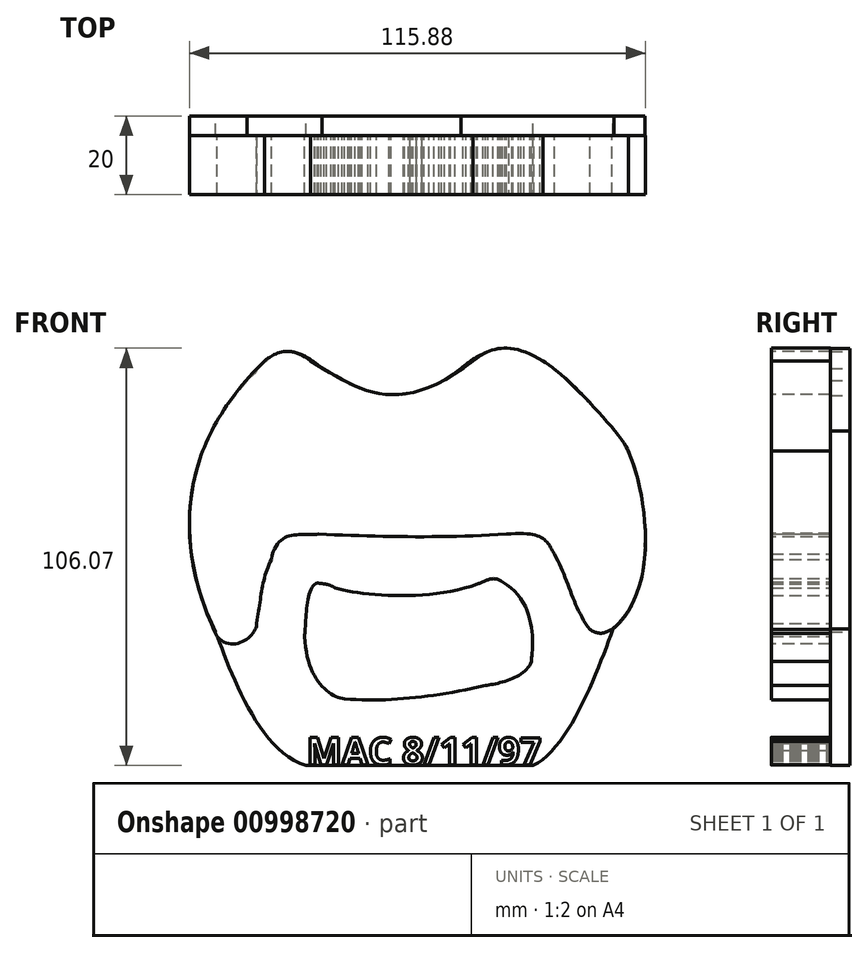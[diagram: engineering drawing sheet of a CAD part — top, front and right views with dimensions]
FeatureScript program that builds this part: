
annotation { "Feature Type Name" : "Feature", "Feature Type Description" : "" }
export const myFeature = defineFeature(function(context is Context, id is Id, definition is map)
    precondition{}
    {
        {
            var Q0;
            Q0=qCreatedBy(makeId("Front.planeOp"),FACE);
            var sketch = newSketch(context, id + "F0", { "sketchPlane" : qUnion([Q0])});
            skFitSpline(sketch, "E0", {"points": [v(-49.64, -27.93) * mm, v(-26.72, -61.84) * mm], "startDerivative": vector(11.72, -30.39) * mm, "endDerivative": vector(37.33, -12.16) * mm});
            skFitSpline(sketch, "E1", {"points": [v(31.01, -61.84) * mm, v(51.28, -27.15) * mm], "startDerivative": vector(27.78, 13.75) * mm, "endDerivative": vector(11.84, 32.53) * mm});
            skLineSegment(sketch, "E2", {"start": v(-26.72, -61.84) * mm, "end": v(31.01, -61.84) * mm});
            skFitSpline(sketch, "E3", {"points": [v(51.28, -27.15) * mm, v(51.52, 23.23) * mm], "startDerivative": vector(41.62, 33.95) * mm, "endDerivative": vector(-20.8, 17.52) * mm});
            skFitSpline(sketch, "E4", {"points": [v(12.65, 39.05) * mm, v(-22.58, 39.05) * mm], "startDerivative": vector(-37.96, -29.68) * mm, "endDerivative": vector(-36.87, 25.55) * mm});
            skFitSpline(sketch, "E5", {"points": [v(-22.58, 39.05) * mm, v(-41.69, 36) * mm], "startDerivative": vector(-32.12, 28.1) * mm, "endDerivative": vector(-14.5, -12.95) * mm});
            skFitSpline(sketch, "E6", {"points": [v(-41.69, 36) * mm, v(-49.64, -27.93) * mm], "startDerivative": vector(-69.09, -76.85) * mm, "endDerivative": vector(16.3, -33.38) * mm});
            skFitSpline(sketch, "E7", {"points": [v(12.65, 39.05) * mm, v(51.52, 23.23) * mm], "startDerivative": vector(34.23, 29.82) * mm, "endDerivative": vector(52.2, -63.88) * mm});
            skSolve(sketch);
        }
        {
            var Q0;
            Q0 = qSketchRegion(id + "F0", true);
            extrude(context, id + "F1", {"entities" : qUnion([Q0]), "depth" : 5 * mm, "offsetDistance" : 25 * mm});
        }
        {
            var Q0;
            {var subQ0=sQuery(id+"F0.wireOp",EDGE,"E1");var subQ1=sQuery(id+"F0.wireOp",EDGE,"E3");var subQ2=sQuery(id+"F0.wireOp",EDGE,"E0");var subQ3=sQuery(id+"F0.wireOp",EDGE,"E4");var subQ4=sQuery(id+"F0.wireOp",EDGE,"E5");var subQ5=sQuery(id+"F0.wireOp",EDGE,"E6");var subQ6=sQuery(id+"F0.wireOp",EDGE,"E7");var subQ7=sQuery(id+"F0.wireOp",EDGE,"E2");Q0=makeQuery(id+"F8dBhZbgDJk9qM2_3.boolean.opBoolean","SPLIT",FACE,{"disambiguationData":[TD([makeQuery(id+"F1.opExtrude","SWEPT_FACE",FACE,{"disambiguationData":[OSD([subQ2])]})])],"derivedFrom":makeQuery(id+"F1.opExtrude","CAP_FACE",FACE,{"disambiguationData":[OSD([subQ2,subQ0,subQ7,subQ1,subQ3,subQ4,subQ5,subQ6])],"isStart":false})});}
            var sketch = newSketch(context, id + "F2", { "sketchPlane" : qUnion([Q0])});
            skFitSpline(sketch, "E8", {"points": [v(-49.27, -29.03) * mm, v(-37.25, 40.91) * mm], "startDerivative": vector(-29.9, 61.13) * mm, "endDerivative": vector(72.6, 69.68) * mm});
            skFitSpline(sketch, "E9", {"points": [v(-37.25, 40.91) * mm, v(-25.54, 40.91) * mm], "startDerivative": vector(6.02, 5.53) * mm, "endDerivative": vector(16.1, -13.33) * mm});
            skFitSpline(sketch, "E10", {"points": [v(-25.54, 40.91) * mm, v(15.7, 40.91) * mm], "startDerivative": vector(38.22, -23.1) * mm, "endDerivative": vector(57.56, 43.58) * mm});
            skFitSpline(sketch, "E11", {"points": [v(15.7, 40.91) * mm, v(33.49, 40.91) * mm], "startDerivative": vector(9.43, 8.13) * mm, "endDerivative": vector(26.98, -17.55) * mm});
            skFitSpline(sketch, "E12", {"points": [v(33.49, 40.91) * mm, v(55.17, 18.05) * mm], "startDerivative": vector(14.45, -7.12) * mm, "endDerivative": vector(3.1, -10.98) * mm});
            skFitSpline(sketch, "E13", {"points": [v(55.17, 18.05) * mm, v(50.97, -27.22) * mm], "startDerivative": vector(10.86, -21.75) * mm, "endDerivative": vector(-40.7, -32) * mm});
            skFitSpline(sketch, "E14", {"points": [v(50.97, -27.22) * mm, v(45.4, -27.22) * mm], "startDerivative": vector(-6.75, -3.45) * mm, "endDerivative": vector(-7.4, 4.48) * mm});
            skFitSpline(sketch, "E15", {"points": [v(45.4, -27.22) * mm, v(36.4, -8.1) * mm], "startDerivative": vector(-13.1, 17.23) * mm, "endDerivative": vector(-10.78, 19.3) * mm});
            skFitSpline(sketch, "E16", {"points": [v(36.4, -8.1) * mm, v(24.2, -3.02) * mm], "startDerivative": vector(-5.92, 9.84) * mm, "endDerivative": vector(-29.5, -2.46) * mm});
            skFitSpline(sketch, "E17", {"points": [v(24.2, -3.02) * mm, v(-23.47, -3.02) * mm], "startDerivative": vector(-48.76, -3.28) * mm, "endDerivative": vector(-46.71, 2.05) * mm});
            skFitSpline(sketch, "E18", {"points": [v(-23.47, -3.02) * mm, v(-35.52, -9.48) * mm], "startDerivative": vector(-13.93, -1.64) * mm, "endDerivative": vector(-4.59, -24.32) * mm});
            skFitSpline(sketch, "E19", {"points": [v(-35.52, -9.48) * mm, v(-39.3, -25.66) * mm], "startDerivative": vector(-7.7, -15.02) * mm, "endDerivative": vector(-3.65, -17.94) * mm});
            skFitSpline(sketch, "E20", {"points": [v(-39.3, -25.66) * mm, v(-49.27, -29.03) * mm], "startDerivative": vector(1.6, -8.56) * mm, "endDerivative": vector(-11.92, 14.24) * mm});
            skFitSpline(sketch, "E21", {"points": [v(23.15, -15.2) * mm, v(30.55, -35.42) * mm], "startDerivative": vector(28.28, -15.2) * mm, "endDerivative": vector(-0.65, -8.25) * mm});
            skFitSpline(sketch, "E22", {"points": [v(30.55, -35.42) * mm, v(18.86, -41.5) * mm], "startDerivative": vector(-4.34, -12.59) * mm, "endDerivative": vector(-9.87, -1.38) * mm});
            skFitSpline(sketch, "E23", {"points": [v(18.86, -41.5) * mm, v(-16.94, -44.93) * mm], "startDerivative": vector(-39.56, -9.03) * mm, "endDerivative": vector(-34.32, 2.28) * mm});
            skFitSpline(sketch, "E24", {"points": [v(-16.94, -44.93) * mm, v(-27.09, -29.03) * mm], "startDerivative": vector(-12.51, 1.95) * mm, "endDerivative": vector(-1.69, 32.43) * mm});
            skFitSpline(sketch, "E25", {"points": [v(-27.09, -29.03) * mm, v(-23.74, -15.46) * mm], "startDerivative": vector(1.36, 7.9) * mm, "endDerivative": vector(10.08, 2.28) * mm});
            skFitSpline(sketch, "E26", {"points": [v(23.15, -15.2) * mm, v(16.82, -15.7) * mm], "startDerivative": vector(-6.45, 5.61) * mm, "endDerivative": vector(-6.21, -2.07) * mm});
            skFitSpline(sketch, "E27", {"points": [v(16.82, -15.7) * mm, v(-19.29, -16.75) * mm], "startDerivative": vector(-37.06, -13.73) * mm, "endDerivative": vector(-20.3, 5.6) * mm});
            skFitSpline(sketch, "E28", {"points": [v(-19.29, -16.75) * mm, v(-23.74, -15.46) * mm], "startDerivative": vector(-3.87, 3.1) * mm, "endDerivative": vector(-4.53, 0.65) * mm});
            skSolve(sketch);
        }
        {
            var Q0;
            Q0 = qSketchRegion(id + "F2", true);
            extrude(context, id + "F3", {"entities" : qUnion([Q0]), "depth" : 15 * mm, "offsetDistance" : 25 * mm});
        }
        {
            var Q0;
            Q0=makeQuery(id+"F1.opExtrude","CAP_FACE",FACE,{"disambiguationData":[OSD([sQuery(id+"F0.wireOp",EDGE,"E0"),sQuery(id+"F0.wireOp",EDGE,"E1"),sQuery(id+"F0.wireOp",EDGE,"E2"),sQuery(id+"F0.wireOp",EDGE,"E3"),sQuery(id+"F0.wireOp",EDGE,"E4"),sQuery(id+"F0.wireOp",EDGE,"E5"),sQuery(id+"F0.wireOp",EDGE,"E6"),sQuery(id+"F0.wireOp",EDGE,"E7")])],"isStart":false});
            var sketch = newSketch(context, id + "F4", { "sketchPlane" : qUnion([Q0])});
            skText(sketch, "E29", { "text": "MAC 8/11/97", "fontName": "OpenSans-Bold.ttf"});
            const initialGuessF4  = {"E29": [-0.0266, -0.0616, 1, 0, 0.00692]};
            skSetInitialGuess(sketch, initialGuessF4);
            skSolve(sketch);
        }
        {
            var Q0;
            Q0 = qSketchRegion(id + "F4", true);
            extrude(context, id + "F5", {"entities" : qUnion([Q0]), "operationType" : NewBodyOperationType.ADD, "depth" : 15 * mm, "offsetDistance" : 25 * mm});
        }
    });
